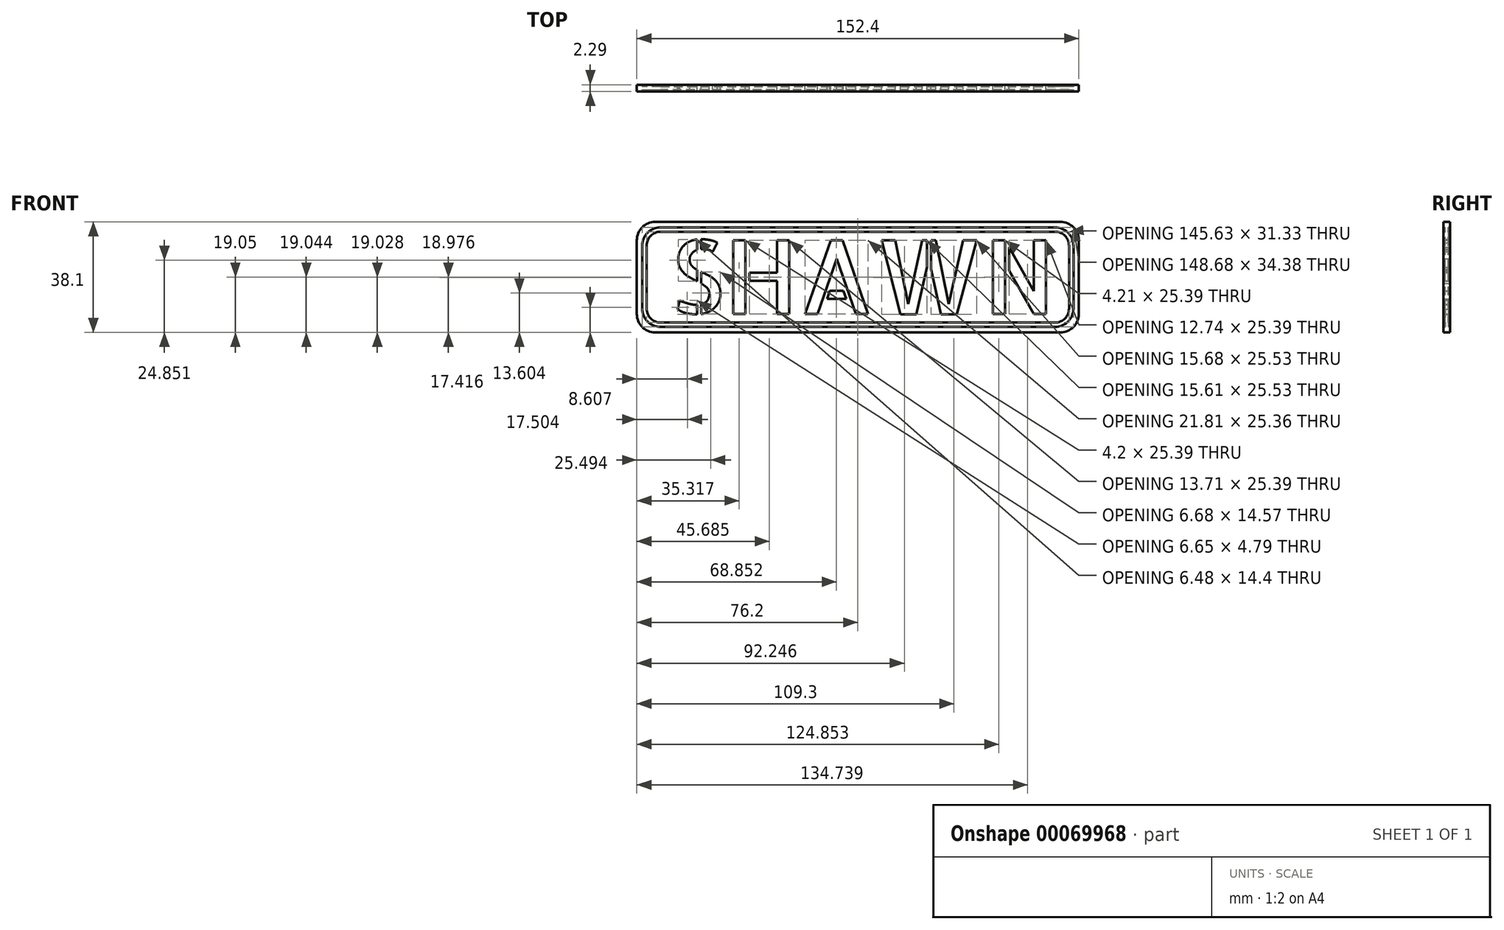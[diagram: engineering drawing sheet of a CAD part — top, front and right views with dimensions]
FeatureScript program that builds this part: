
annotation { "Feature Type Name" : "Feature", "Feature Type Description" : "" }
export const myFeature = defineFeature(function(context is Context, id is Id, definition is map)
    precondition{}
    {
        {
            var Q0;
            Q0=qCreatedBy(makeId("Front.planeOp"),FACE);
            var sketch = newSketch(context, id + "F0", { "sketchPlane" : qUnion([Q0])});
            skLineSegment(sketch, "E0.rect.bottom", {"start": v(69.85, -19.05) * mm, "end": v(-69.85, -19.05) * mm});
            skLineSegment(sketch, "E0.rect.top", {"start": v(69.85, 19.05) * mm, "end": v(-69.85, 19.05) * mm});
            skLineSegment(sketch, "E0.rect.left", {"start": v(76.2, -12.7) * mm, "end": v(76.2, 12.7) * mm});
            skLineSegment(sketch, "E0.rect.right", {"start": v(-76.2, -12.7) * mm, "end": v(-76.2, 12.7) * mm});
            skPoint(sketch, "E0.rect.middle", {"position": v(0, 0) * mm});
            skPoint(sketch, "E1.visualSharp", {"position": v(-76.2, 19.05) * mm});
            skArc(sketch, "E1.filletArc", {"start": v(-69.85, 19.05) * mm, "mid": v(-74.34, 17.2) * mm, "end": v(-76.2, 12.7) * mm});
            skPoint(sketch, "E2.visualSharp", {"position": v(-76.2, -19.05) * mm});
            skArc(sketch, "E2.filletArc", {"start": v(-76.2, -12.7) * mm, "mid": v(-74.34, -17.2) * mm, "end": v(-69.85, -19.05) * mm});
            skPoint(sketch, "E3.visualSharp", {"position": v(76.2, -19.05) * mm});
            skArc(sketch, "E3.filletArc", {"start": v(69.85, -19.05) * mm, "mid": v(74.34, -17.2) * mm, "end": v(76.2, -12.7) * mm});
            skPoint(sketch, "E4.visualSharp", {"position": v(76.2, 19.05) * mm});
            skArc(sketch, "E4.filletArc", {"start": v(76.2, 12.7) * mm, "mid": v(74.34, 17.2) * mm, "end": v(69.85, 19.05) * mm});
            skText(sketch, "E5", { "text": "SHAWN", "fontName": "AllertaStencil-Regular.ttf"});
            skLineSegment(sketch, "E6", {"start": v(-64.9, 0) * mm, "end": v(-76.2, 0) * mm});
            skLineSegment(sketch, "E7", {"start": v(64.9, 0) * mm, "end": v(76.2, 0) * mm});
            const initialGuessF0  = {"E5": [-0.0649, -0.0127, 1, 0, 0.0254]};
            skSetInitialGuess(sketch, initialGuessF0);
            skSolve(sketch);
        }
        {
            var Q0;
            Q0=makeQuery(id+"F0.imprint","IMPRINT",FACE,{"disambiguationData":[TD([[makeQuery(id+"F0.imprint","IMPRINT",EDGE,{"derivedFrom":sQuery(id+"F0.wireOp",EDGE,"E0.rect.bottom")}),-1.0]])]});
            extrude(context, id + "F1", {"entities" : qUnion([Q0]), "depth" : 1.02 * mm});
        }
        {
            var Q0;
            Q0=makeQuery(id+"F1.opExtrude","CAP_FACE",FACE,{"disambiguationData":[OSD([sQuery(id+"F0.wireOp",EDGE,"E0.rect.bottom"),sQuery(id+"F0.wireOp",EDGE,"E0.rect.top"),sQuery(id+"F0.wireOp",EDGE,"E0.rect.left"),sQuery(id+"F0.wireOp",EDGE,"E0.rect.right"),sQuery(id+"F0.wireOp",EDGE,"E1.filletArc"),sQuery(id+"F0.wireOp",EDGE,"E2.filletArc"),sQuery(id+"F0.wireOp",EDGE,"E3.filletArc"),sQuery(id+"F0.wireOp",EDGE,"E4.filletArc"),sQuery(id+"F0.wireOp",EDGE,"E5.sketch_text.stroke-0"),sQuery(id+"F0.wireOp",EDGE,"E5.sketch_text.stroke-1"),sQuery(id+"F0.wireOp",EDGE,"E5.sketch_text.stroke-2"),sQuery(id+"F0.wireOp",EDGE,"E5.sketch_text.stroke-3"),sQuery(id+"F0.wireOp",EDGE,"E5.sketch_text.stroke-4"),sQuery(id+"F0.wireOp",EDGE,"E5.sketch_text.stroke-5"),sQuery(id+"F0.wireOp",EDGE,"E5.sketch_text.stroke-6"),sQuery(id+"F0.wireOp",EDGE,"E5.sketch_text.stroke-7"),sQuery(id+"F0.wireOp",EDGE,"E5.sketch_text.stroke-8"),sQuery(id+"F0.wireOp",EDGE,"E5.sketch_text.stroke-9"),sQuery(id+"F0.wireOp",EDGE,"E5.sketch_text.stroke-10"),sQuery(id+"F0.wireOp",EDGE,"E5.sketch_text.stroke-11"),sQuery(id+"F0.wireOp",EDGE,"E5.sketch_text.stroke-12"),sQuery(id+"F0.wireOp",EDGE,"E5.sketch_text.stroke-13"),sQuery(id+"F0.wireOp",EDGE,"E5.sketch_text.stroke-14"),sQuery(id+"F0.wireOp",EDGE,"E5.sketch_text.stroke-15"),sQuery(id+"F0.wireOp",EDGE,"E5.sketch_text.stroke-16"),sQuery(id+"F0.wireOp",EDGE,"E5.sketch_text.stroke-17"),sQuery(id+"F0.wireOp",EDGE,"E5.sketch_text.stroke-18"),sQuery(id+"F0.wireOp",EDGE,"E5.sketch_text.stroke-19"),sQuery(id+"F0.wireOp",EDGE,"E5.sketch_text.stroke-20"),sQuery(id+"F0.wireOp",EDGE,"E5.sketch_text.stroke-21"),sQuery(id+"F0.wireOp",EDGE,"E5.sketch_text.stroke-22"),sQuery(id+"F0.wireOp",EDGE,"E5.sketch_text.stroke-23"),sQuery(id+"F0.wireOp",EDGE,"E5.sketch_text.stroke-24"),sQuery(id+"F0.wireOp",EDGE,"E5.sketch_text.stroke-25"),sQuery(id+"F0.wireOp",EDGE,"E5.sketch_text.stroke-26"),sQuery(id+"F0.wireOp",EDGE,"E5.sketch_text.stroke-27"),sQuery(id+"F0.wireOp",EDGE,"E5.sketch_text.stroke-28"),sQuery(id+"F0.wireOp",EDGE,"E5.sketch_text.stroke-29"),sQuery(id+"F0.wireOp",EDGE,"E5.sketch_text.stroke-30"),sQuery(id+"F0.wireOp",EDGE,"E5.sketch_text.stroke-31"),sQuery(id+"F0.wireOp",EDGE,"E5.sketch_text.stroke-32"),sQuery(id+"F0.wireOp",EDGE,"E5.sketch_text.stroke-33"),sQuery(id+"F0.wireOp",EDGE,"E5.sketch_text.stroke-34"),sQuery(id+"F0.wireOp",EDGE,"E5.sketch_text.stroke-35"),sQuery(id+"F0.wireOp",EDGE,"E5.sketch_text.stroke-36"),sQuery(id+"F0.wireOp",EDGE,"E5.sketch_text.stroke-37"),sQuery(id+"F0.wireOp",EDGE,"E5.sketch_text.stroke-38"),sQuery(id+"F0.wireOp",EDGE,"E5.sketch_text.stroke-39"),sQuery(id+"F0.wireOp",EDGE,"E5.sketch_text.stroke-40"),sQuery(id+"F0.wireOp",EDGE,"E5.sketch_text.stroke-41"),sQuery(id+"F0.wireOp",EDGE,"E5.sketch_text.stroke-42"),sQuery(id+"F0.wireOp",EDGE,"E5.sketch_text.stroke-43"),sQuery(id+"F0.wireOp",EDGE,"E5.sketch_text.stroke-44"),sQuery(id+"F0.wireOp",EDGE,"E5.sketch_text.stroke-45"),sQuery(id+"F0.wireOp",EDGE,"E5.sketch_text.stroke-46"),sQuery(id+"F0.wireOp",EDGE,"E5.sketch_text.stroke-47"),sQuery(id+"F0.wireOp",EDGE,"E5.sketch_text.stroke-48"),sQuery(id+"F0.wireOp",EDGE,"E5.sketch_text.stroke-49"),sQuery(id+"F0.wireOp",EDGE,"E5.sketch_text.stroke-50"),sQuery(id+"F0.wireOp",EDGE,"E5.sketch_text.stroke-51"),sQuery(id+"F0.wireOp",EDGE,"E5.sketch_text.stroke-52"),sQuery(id+"F0.wireOp",EDGE,"E5.sketch_text.stroke-53"),sQuery(id+"F0.wireOp",EDGE,"E5.sketch_text.stroke-54"),sQuery(id+"F0.wireOp",EDGE,"E5.sketch_text.stroke-55"),sQuery(id+"F0.wireOp",EDGE,"E5.sketch_text.stroke-56"),sQuery(id+"F0.wireOp",EDGE,"E5.sketch_text.stroke-57"),sQuery(id+"F0.wireOp",EDGE,"E5.sketch_text.stroke-58"),sQuery(id+"F0.wireOp",EDGE,"E5.sketch_text.stroke-59"),sQuery(id+"F0.wireOp",EDGE,"E5.sketch_text.stroke-60"),sQuery(id+"F0.wireOp",EDGE,"E5.sketch_text.stroke-61"),sQuery(id+"F0.wireOp",EDGE,"E5.sketch_text.stroke-62"),sQuery(id+"F0.wireOp",EDGE,"E5.sketch_text.stroke-63"),sQuery(id+"F0.wireOp",EDGE,"E5.sketch_text.stroke-64"),sQuery(id+"F0.wireOp",EDGE,"E5.sketch_text.stroke-65"),sQuery(id+"F0.wireOp",EDGE,"E5.sketch_text.stroke-66"),sQuery(id+"F0.wireOp",EDGE,"E5.sketch_text.stroke-67"),sQuery(id+"F0.wireOp",EDGE,"E5.sketch_text.stroke-68"),sQuery(id+"F0.wireOp",EDGE,"E5.sketch_text.stroke-69"),sQuery(id+"F0.wireOp",EDGE,"E5.sketch_text.stroke-70"),sQuery(id+"F0.wireOp",EDGE,"E5.sketch_text.stroke-71"),sQuery(id+"F0.wireOp",EDGE,"E5.sketch_text.stroke-72"),sQuery(id+"F0.wireOp",EDGE,"E5.sketch_text.stroke-73"),sQuery(id+"F0.wireOp",EDGE,"E5.sketch_text.stroke-74"),sQuery(id+"F0.wireOp",EDGE,"E5.sketch_text.stroke-75"),sQuery(id+"F0.wireOp",EDGE,"E5.sketch_text.stroke-76"),sQuery(id+"F0.wireOp",EDGE,"E5.sketch_text.stroke-77"),sQuery(id+"F0.wireOp",EDGE,"E5.sketch_text.stroke-78"),sQuery(id+"F0.wireOp",EDGE,"E5.sketch_text.stroke-79"),sQuery(id+"F0.wireOp",EDGE,"E5.sketch_text.stroke-80"),sQuery(id+"F0.wireOp",EDGE,"E5.sketch_text.stroke-81"),sQuery(id+"F0.wireOp",EDGE,"E5.sketch_text.stroke-82"),sQuery(id+"F0.wireOp",EDGE,"E5.sketch_text.stroke-83"),sQuery(id+"F0.wireOp",EDGE,"E5.sketch_text.stroke-84"),sQuery(id+"F0.wireOp",EDGE,"E5.sketch_text.stroke-85"),sQuery(id+"F0.wireOp",EDGE,"E5.sketch_text.stroke-86"),sQuery(id+"F0.wireOp",EDGE,"E5.sketch_text.stroke-87"),sQuery(id+"F0.wireOp",EDGE,"E5.sketch_text.stroke-88"),sQuery(id+"F0.wireOp",EDGE,"E5.sketch_text.stroke-89"),sQuery(id+"F0.wireOp",EDGE,"E5.sketch_text.stroke-90"),sQuery(id+"F0.wireOp",EDGE,"E5.sketch_text.stroke-91"),sQuery(id+"F0.wireOp",EDGE,"E5.sketch_text.stroke-92"),sQuery(id+"F0.wireOp",EDGE,"E5.sketch_text.stroke-93"),sQuery(id+"F0.wireOp",EDGE,"E5.sketch_text.stroke-94"),sQuery(id+"F0.wireOp",EDGE,"E5.sketch_text.stroke-95"),sQuery(id+"F0.wireOp",EDGE,"E5.sketch_text.stroke-96"),sQuery(id+"F0.wireOp",EDGE,"E5.sketch_text.stroke-97"),sQuery(id+"F0.wireOp",EDGE,"E5.sketch_text.stroke-98"),sQuery(id+"F0.wireOp",EDGE,"E5.sketch_text.stroke-99")])],"isStart":false});
            var sketch = newSketch(context, id + "F2", { "sketchPlane" : qUnion([Q0])});
            skLineSegment(sketch, "E8.rect.bottom", {"start": v(68, -17.2) * mm, "end": v(-68, -17.2) * mm});
            skLineSegment(sketch, "E8.rect.top", {"start": v(68, 17.2) * mm, "end": v(-68, 17.2) * mm});
            skLineSegment(sketch, "E8.rect.left", {"start": v(74.34, -10.84) * mm, "end": v(74.34, 10.84) * mm});
            skLineSegment(sketch, "E8.rect.right", {"start": v(-74.34, -10.84) * mm, "end": v(-74.34, 10.84) * mm});
            skPoint(sketch, "E8.rect.middle", {"position": v(0, 0) * mm});
            skPoint(sketch, "E9.visualSharp", {"position": v(-74.34, 17.2) * mm});
            skArc(sketch, "E9.filletArc", {"start": v(-68, 17.2) * mm, "mid": v(-72.48, 15.33) * mm, "end": v(-74.34, 10.84) * mm});
            skPoint(sketch, "E10.visualSharp", {"position": v(-74.34, -17.2) * mm});
            skArc(sketch, "E10.filletArc", {"start": v(-74.34, -10.84) * mm, "mid": v(-72.48, -15.33) * mm, "end": v(-68, -17.2) * mm});
            skPoint(sketch, "E11.visualSharp", {"position": v(74.34, -17.2) * mm});
            skArc(sketch, "E11.filletArc", {"start": v(68, -17.2) * mm, "mid": v(72.48, -15.33) * mm, "end": v(74.34, -10.84) * mm});
            skPoint(sketch, "E12.visualSharp", {"position": v(74.34, 17.2) * mm});
            skArc(sketch, "E12.filletArc", {"start": v(74.34, 10.84) * mm, "mid": v(72.48, 15.33) * mm, "end": v(68, 17.2) * mm});
            skArc(sketch, "E13.0", {"start": v(72.82, 10.84) * mm, "mid": v(71.4, 14.25) * mm, "end": v(68, 15.67) * mm});
            skLineSegment(sketch, "E13.1", {"start": v(72.82, -10.84) * mm, "end": v(72.82, 10.84) * mm});
            skLineSegment(sketch, "E13.2", {"start": v(68, 15.67) * mm, "end": v(-68, 15.67) * mm});
            skArc(sketch, "E13.3", {"start": v(68, -15.67) * mm, "mid": v(71.4, -14.25) * mm, "end": v(72.82, -10.84) * mm});
            skArc(sketch, "E13.4", {"start": v(-68, 15.67) * mm, "mid": v(-71.4, 14.25) * mm, "end": v(-72.82, 10.84) * mm});
            skLineSegment(sketch, "E13.5", {"start": v(-72.82, -10.84) * mm, "end": v(-72.82, 10.84) * mm});
            skArc(sketch, "E13.6", {"start": v(-72.82, -10.84) * mm, "mid": v(-71.4, -14.25) * mm, "end": v(-68, -15.67) * mm});
            skLineSegment(sketch, "E13.7", {"start": v(68, -15.67) * mm, "end": v(-68, -15.67) * mm});
            skSolve(sketch);
        }
        {
            var Q0;
            Q0=makeQuery(id+"F2.imprint","IMPRINT",FACE,{"disambiguationData":[TD([[makeQuery(id+"F2.imprint","IMPRINT",EDGE,{"derivedFrom":sQuery(id+"F2.wireOp",EDGE,"E8.rect.bottom")}),1.0]])]});
            var Q1;
            Q1=makeQuery(id+"F2.imprint","IMPRINT",FACE,{"disambiguationData":[TD([[makeQuery(id+"F2.imprint","IMPRINT",EDGE,{"derivedFrom":sQuery(id+"F2.wireOp",EDGE,"E13.0")}),1.0]])]});
            extrude(context, id + "F3", {"entities" : qUnion([Q0, Q1]), "operationType" : NewBodyOperationType.ADD, "depth" : 0.64 * mm});
        }
        {
            var Q0;
            Q0=makeQuery(id+"F1.opExtrude","CAP_FACE",FACE,{"disambiguationData":[OSD([sQuery(id+"F0.wireOp",EDGE,"E0.rect.bottom"),sQuery(id+"F0.wireOp",EDGE,"E0.rect.top"),sQuery(id+"F0.wireOp",EDGE,"E0.rect.left"),sQuery(id+"F0.wireOp",EDGE,"E0.rect.right"),sQuery(id+"F0.wireOp",EDGE,"E1.filletArc"),sQuery(id+"F0.wireOp",EDGE,"E2.filletArc"),sQuery(id+"F0.wireOp",EDGE,"E3.filletArc"),sQuery(id+"F0.wireOp",EDGE,"E4.filletArc"),sQuery(id+"F0.wireOp",EDGE,"E5.sketch_text.stroke-0"),sQuery(id+"F0.wireOp",EDGE,"E5.sketch_text.stroke-1"),sQuery(id+"F0.wireOp",EDGE,"E5.sketch_text.stroke-2"),sQuery(id+"F0.wireOp",EDGE,"E5.sketch_text.stroke-3"),sQuery(id+"F0.wireOp",EDGE,"E5.sketch_text.stroke-4"),sQuery(id+"F0.wireOp",EDGE,"E5.sketch_text.stroke-5"),sQuery(id+"F0.wireOp",EDGE,"E5.sketch_text.stroke-6"),sQuery(id+"F0.wireOp",EDGE,"E5.sketch_text.stroke-7"),sQuery(id+"F0.wireOp",EDGE,"E5.sketch_text.stroke-8"),sQuery(id+"F0.wireOp",EDGE,"E5.sketch_text.stroke-9"),sQuery(id+"F0.wireOp",EDGE,"E5.sketch_text.stroke-10"),sQuery(id+"F0.wireOp",EDGE,"E5.sketch_text.stroke-11"),sQuery(id+"F0.wireOp",EDGE,"E5.sketch_text.stroke-12"),sQuery(id+"F0.wireOp",EDGE,"E5.sketch_text.stroke-13"),sQuery(id+"F0.wireOp",EDGE,"E5.sketch_text.stroke-14"),sQuery(id+"F0.wireOp",EDGE,"E5.sketch_text.stroke-15"),sQuery(id+"F0.wireOp",EDGE,"E5.sketch_text.stroke-16"),sQuery(id+"F0.wireOp",EDGE,"E5.sketch_text.stroke-17"),sQuery(id+"F0.wireOp",EDGE,"E5.sketch_text.stroke-18"),sQuery(id+"F0.wireOp",EDGE,"E5.sketch_text.stroke-19"),sQuery(id+"F0.wireOp",EDGE,"E5.sketch_text.stroke-20"),sQuery(id+"F0.wireOp",EDGE,"E5.sketch_text.stroke-21"),sQuery(id+"F0.wireOp",EDGE,"E5.sketch_text.stroke-22"),sQuery(id+"F0.wireOp",EDGE,"E5.sketch_text.stroke-23"),sQuery(id+"F0.wireOp",EDGE,"E5.sketch_text.stroke-24"),sQuery(id+"F0.wireOp",EDGE,"E5.sketch_text.stroke-25"),sQuery(id+"F0.wireOp",EDGE,"E5.sketch_text.stroke-26"),sQuery(id+"F0.wireOp",EDGE,"E5.sketch_text.stroke-27"),sQuery(id+"F0.wireOp",EDGE,"E5.sketch_text.stroke-28"),sQuery(id+"F0.wireOp",EDGE,"E5.sketch_text.stroke-29"),sQuery(id+"F0.wireOp",EDGE,"E5.sketch_text.stroke-30"),sQuery(id+"F0.wireOp",EDGE,"E5.sketch_text.stroke-31"),sQuery(id+"F0.wireOp",EDGE,"E5.sketch_text.stroke-32"),sQuery(id+"F0.wireOp",EDGE,"E5.sketch_text.stroke-33"),sQuery(id+"F0.wireOp",EDGE,"E5.sketch_text.stroke-34"),sQuery(id+"F0.wireOp",EDGE,"E5.sketch_text.stroke-35"),sQuery(id+"F0.wireOp",EDGE,"E5.sketch_text.stroke-36"),sQuery(id+"F0.wireOp",EDGE,"E5.sketch_text.stroke-37"),sQuery(id+"F0.wireOp",EDGE,"E5.sketch_text.stroke-38"),sQuery(id+"F0.wireOp",EDGE,"E5.sketch_text.stroke-39"),sQuery(id+"F0.wireOp",EDGE,"E5.sketch_text.stroke-40"),sQuery(id+"F0.wireOp",EDGE,"E5.sketch_text.stroke-41"),sQuery(id+"F0.wireOp",EDGE,"E5.sketch_text.stroke-42"),sQuery(id+"F0.wireOp",EDGE,"E5.sketch_text.stroke-43"),sQuery(id+"F0.wireOp",EDGE,"E5.sketch_text.stroke-44"),sQuery(id+"F0.wireOp",EDGE,"E5.sketch_text.stroke-45"),sQuery(id+"F0.wireOp",EDGE,"E5.sketch_text.stroke-46"),sQuery(id+"F0.wireOp",EDGE,"E5.sketch_text.stroke-47"),sQuery(id+"F0.wireOp",EDGE,"E5.sketch_text.stroke-48"),sQuery(id+"F0.wireOp",EDGE,"E5.sketch_text.stroke-49"),sQuery(id+"F0.wireOp",EDGE,"E5.sketch_text.stroke-50"),sQuery(id+"F0.wireOp",EDGE,"E5.sketch_text.stroke-51"),sQuery(id+"F0.wireOp",EDGE,"E5.sketch_text.stroke-52"),sQuery(id+"F0.wireOp",EDGE,"E5.sketch_text.stroke-53"),sQuery(id+"F0.wireOp",EDGE,"E5.sketch_text.stroke-54"),sQuery(id+"F0.wireOp",EDGE,"E5.sketch_text.stroke-55"),sQuery(id+"F0.wireOp",EDGE,"E5.sketch_text.stroke-56"),sQuery(id+"F0.wireOp",EDGE,"E5.sketch_text.stroke-57"),sQuery(id+"F0.wireOp",EDGE,"E5.sketch_text.stroke-58"),sQuery(id+"F0.wireOp",EDGE,"E5.sketch_text.stroke-59"),sQuery(id+"F0.wireOp",EDGE,"E5.sketch_text.stroke-60"),sQuery(id+"F0.wireOp",EDGE,"E5.sketch_text.stroke-61"),sQuery(id+"F0.wireOp",EDGE,"E5.sketch_text.stroke-62"),sQuery(id+"F0.wireOp",EDGE,"E5.sketch_text.stroke-63"),sQuery(id+"F0.wireOp",EDGE,"E5.sketch_text.stroke-64"),sQuery(id+"F0.wireOp",EDGE,"E5.sketch_text.stroke-65"),sQuery(id+"F0.wireOp",EDGE,"E5.sketch_text.stroke-66"),sQuery(id+"F0.wireOp",EDGE,"E5.sketch_text.stroke-67"),sQuery(id+"F0.wireOp",EDGE,"E5.sketch_text.stroke-68"),sQuery(id+"F0.wireOp",EDGE,"E5.sketch_text.stroke-69"),sQuery(id+"F0.wireOp",EDGE,"E5.sketch_text.stroke-70"),sQuery(id+"F0.wireOp",EDGE,"E5.sketch_text.stroke-71"),sQuery(id+"F0.wireOp",EDGE,"E5.sketch_text.stroke-72"),sQuery(id+"F0.wireOp",EDGE,"E5.sketch_text.stroke-73"),sQuery(id+"F0.wireOp",EDGE,"E5.sketch_text.stroke-74"),sQuery(id+"F0.wireOp",EDGE,"E5.sketch_text.stroke-75"),sQuery(id+"F0.wireOp",EDGE,"E5.sketch_text.stroke-76"),sQuery(id+"F0.wireOp",EDGE,"E5.sketch_text.stroke-77"),sQuery(id+"F0.wireOp",EDGE,"E5.sketch_text.stroke-78"),sQuery(id+"F0.wireOp",EDGE,"E5.sketch_text.stroke-79"),sQuery(id+"F0.wireOp",EDGE,"E5.sketch_text.stroke-80"),sQuery(id+"F0.wireOp",EDGE,"E5.sketch_text.stroke-81"),sQuery(id+"F0.wireOp",EDGE,"E5.sketch_text.stroke-82"),sQuery(id+"F0.wireOp",EDGE,"E5.sketch_text.stroke-83"),sQuery(id+"F0.wireOp",EDGE,"E5.sketch_text.stroke-84"),sQuery(id+"F0.wireOp",EDGE,"E5.sketch_text.stroke-85"),sQuery(id+"F0.wireOp",EDGE,"E5.sketch_text.stroke-86"),sQuery(id+"F0.wireOp",EDGE,"E5.sketch_text.stroke-87"),sQuery(id+"F0.wireOp",EDGE,"E5.sketch_text.stroke-88"),sQuery(id+"F0.wireOp",EDGE,"E5.sketch_text.stroke-89"),sQuery(id+"F0.wireOp",EDGE,"E5.sketch_text.stroke-90"),sQuery(id+"F0.wireOp",EDGE,"E5.sketch_text.stroke-91"),sQuery(id+"F0.wireOp",EDGE,"E5.sketch_text.stroke-92"),sQuery(id+"F0.wireOp",EDGE,"E5.sketch_text.stroke-93"),sQuery(id+"F0.wireOp",EDGE,"E5.sketch_text.stroke-94"),sQuery(id+"F0.wireOp",EDGE,"E5.sketch_text.stroke-95"),sQuery(id+"F0.wireOp",EDGE,"E5.sketch_text.stroke-96"),sQuery(id+"F0.wireOp",EDGE,"E5.sketch_text.stroke-97"),sQuery(id+"F0.wireOp",EDGE,"E5.sketch_text.stroke-98"),sQuery(id+"F0.wireOp",EDGE,"E5.sketch_text.stroke-99")])],"isStart":true});
            var sketch = newSketch(context, id + "F4", { "sketchPlane" : qUnion([Q0])});
            skLineSegment(sketch, "E14.rect.bottom", {"start": v(68, -17.2) * mm, "end": v(-68, -17.2) * mm});
            skLineSegment(sketch, "E14.rect.top", {"start": v(68, 17.2) * mm, "end": v(-68, 17.2) * mm});
            skLineSegment(sketch, "E14.rect.left", {"start": v(74.34, -10.84) * mm, "end": v(74.34, 10.84) * mm});
            skLineSegment(sketch, "E14.rect.right", {"start": v(-74.34, -10.84) * mm, "end": v(-74.34, 10.84) * mm});
            skPoint(sketch, "E14.rect.middle", {"position": v(0, 0) * mm});
            skPoint(sketch, "E15.visualSharp", {"position": v(-74.34, 17.2) * mm});
            skArc(sketch, "E15.filletArc", {"start": v(-68, 17.2) * mm, "mid": v(-72.48, 15.33) * mm, "end": v(-74.34, 10.84) * mm});
            skPoint(sketch, "E16.visualSharp", {"position": v(-74.34, -17.2) * mm});
            skArc(sketch, "E16.filletArc", {"start": v(-74.34, -10.84) * mm, "mid": v(-72.48, -15.33) * mm, "end": v(-68, -17.2) * mm});
            skPoint(sketch, "E17.visualSharp", {"position": v(74.34, -17.2) * mm});
            skArc(sketch, "E17.filletArc", {"start": v(68, -17.2) * mm, "mid": v(72.48, -15.33) * mm, "end": v(74.34, -10.84) * mm});
            skPoint(sketch, "E18.visualSharp", {"position": v(74.34, 17.2) * mm});
            skArc(sketch, "E18.filletArc", {"start": v(74.34, 10.84) * mm, "mid": v(72.48, 15.33) * mm, "end": v(68, 17.2) * mm});
            skArc(sketch, "E19.0", {"start": v(72.82, 10.84) * mm, "mid": v(71.4, 14.25) * mm, "end": v(68, 15.67) * mm});
            skLineSegment(sketch, "E19.1", {"start": v(72.82, -10.84) * mm, "end": v(72.82, 10.84) * mm});
            skLineSegment(sketch, "E19.2", {"start": v(68, 15.67) * mm, "end": v(-68, 15.67) * mm});
            skArc(sketch, "E19.3", {"start": v(68, -15.67) * mm, "mid": v(71.4, -14.25) * mm, "end": v(72.82, -10.84) * mm});
            skArc(sketch, "E19.4", {"start": v(-68, 15.67) * mm, "mid": v(-71.4, 14.25) * mm, "end": v(-72.82, 10.84) * mm});
            skLineSegment(sketch, "E19.5", {"start": v(-72.82, -10.84) * mm, "end": v(-72.82, 10.84) * mm});
            skArc(sketch, "E19.6", {"start": v(-72.82, -10.84) * mm, "mid": v(-71.4, -14.25) * mm, "end": v(-68, -15.67) * mm});
            skLineSegment(sketch, "E19.7", {"start": v(68, -15.67) * mm, "end": v(-68, -15.67) * mm});
            skSolve(sketch);
        }
        {
            var Q0;
            Q0=makeQuery(id+"F4.imprint","IMPRINT",FACE,{"disambiguationData":[TD([[makeQuery(id+"F4.imprint","IMPRINT",EDGE,{"derivedFrom":sQuery(id+"F4.wireOp",EDGE,"E19.0")}),1.0]])]});
            var Q1;
            Q1=makeQuery(id+"F4.imprint","IMPRINT",FACE,{"disambiguationData":[TD([[makeQuery(id+"F4.imprint","IMPRINT",EDGE,{"derivedFrom":sQuery(id+"F4.wireOp",EDGE,"E14.rect.bottom")}),1.0]])]});
            extrude(context, id + "F5", {"entities" : qUnion([Q0, Q1]), "operationType" : NewBodyOperationType.ADD, "depth" : 0.64 * mm});
        }
    });
